# Revit family: TAG3
name_source: partatom
category: Furniture
units: mm (PartAtom-declared; Revit-internal decimal feet)

## family parameters
Always vertical = Yes
Cut with Voids When Loaded = No
OmniClass Number = 23.40.20.00
OmniClass Title = General Furniture and Specialties
Render Appearance Source = Family Geometry
Room Calculation Point = No
Shared = No
Work Plane-Based = No

## types (1)
- LBTYP005
    Cost = 39702 $
    Default Elevation = 0 mm  [stored 0 ft]
    Description = 2 x Upton Configurable Task Chair, 1 x Rutland Perch Chair Height Adjustable - Configurable, 3 x Rutland Perch Chair Height Adjustable - Configurable, 1 x Floor Bookcase (Credenza) on Feet-20Hx42Wx18D, 1 x BF Ped on Feet-Full Depth-18Dx21Hx18W, 1 x Single Door Locker on Feet Left-50H x 12W x 18D, 1 x LB LOUNGE, CORNER, 50 TALL, SOLID BASE, REAR OVERLAY, LEFT, 2 x LB LOUNGE 2 SEAT 50"H X 60"W X 30" SOLID BASE, 1 x Universal Spine Glass Insert Screen - .375 20H x 72W, 8 x Desking L-Bracket Pair (2) Black Brackets, 1 x Encounter PwrBeam Laminate End Panel 48w x 50h for 29"h Mnt, 1 x Encounter PwrBeam Double Sided Powered Spine Kit 72, 1 x Encounter PwrBeam Raceway Endcap Painted, 1 x Encounter PwrBeam Vertical Support (for Storage Top Mnt), 1 x COLLAB TBL, KEY TOP, 2mm, 36Dx48Wx42H, DISC, 1 x TBL, PBL, KNF, 36Dx16H, DISC, GLD, 1 x Rectangular - 2mm Edge - 24D x 60W, 2 x Rectangular - 2mm Edge - 24D x 72W, 2 x U-Channel - 48W, 1 x CBX Full Depth BF Ped 18Dx21Hx18W, 1 x Calibrate Dry Planter 50Hx30Wx12D, 1 x Collaborative Table Wall Mount Kit (4 Black Brackets), 1 x CBX Single Door Locker Left 50h x 12w x 18d
    Exported From CET Designer = Yes
    Manufacturer = AIS
    Model = 4700C
    Show LBTYP005 = Yes
    VisibilityIndex = 0

note: [stored X ft] marks values corroborated as IEEE doubles in the binary element streams (Revit-internal decimal feet)

## geometry (parser evidence)
native form markers: Sweep x2
no freeform markers — native parametric forms only
